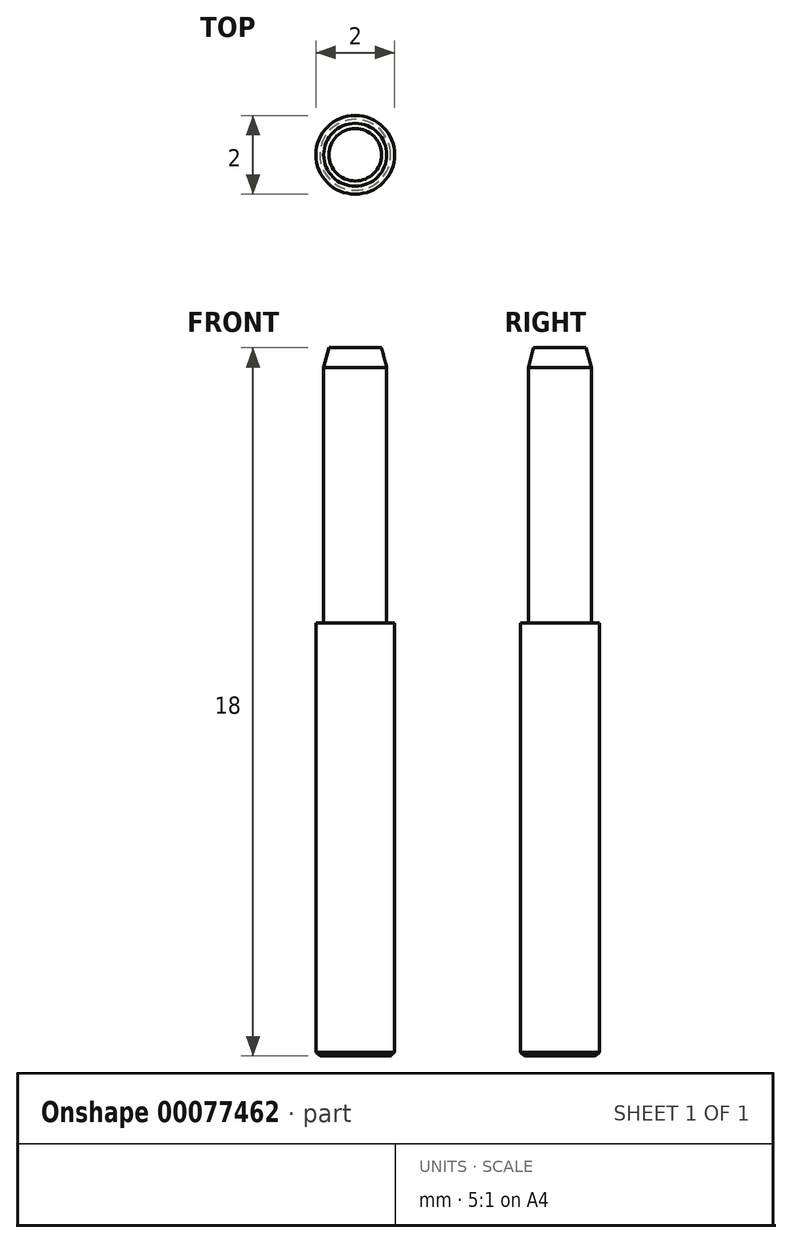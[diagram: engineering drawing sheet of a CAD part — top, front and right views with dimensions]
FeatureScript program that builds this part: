
annotation { "Feature Type Name" : "Feature", "Feature Type Description" : "" }
export const myFeature = defineFeature(function(context is Context, id is Id, definition is map)
    precondition{}
    {
        {
            var Q0;
            Q0=qCreatedBy(makeId("Top.planeOp"),FACE);
            var sketch = newSketch(context, id + "F0", { "sketchPlane" : qUnion([Q0])});
            skCircle(sketch, "E0", {"center": v(0, 0) * mm, "radius": 1 * mm});
            skSolve(sketch);
        }
        {
            var Q0;
            Q0=makeQuery(id+"F0.imprint","IMPRINT",FACE,{"disambiguationData":[TD([[makeQuery(id+"F0.imprint","IMPRINT",EDGE,{"derivedFrom":sQuery(id+"F0.wireOp",EDGE,"E0")}),1.0]])]});
            extrude(context, id + "F1", {"entities" : qUnion([Q0]), "depth" : 11 * mm});
        }
        {
            var Q0;
            Q0=makeQuery(id+"F1.opExtrude","CAP_FACE",FACE,{"disambiguationData":[OSD([sQuery(id+"F0.wireOp",EDGE,"E0")])],"isStart":false});
            var sketch = newSketch(context, id + "F2", { "sketchPlane" : qUnion([Q0])});
            skCircle(sketch, "E1", {"center": v(0, 0) * mm, "radius": 0.8 * mm});
            skSolve(sketch);
        }
        {
            var Q0;
            Q0=makeQuery(id+"F2.imprint","IMPRINT",FACE,{"disambiguationData":[TD([[makeQuery(id+"F2.imprint","IMPRINT",EDGE,{"derivedFrom":sQuery(id+"F2.wireOp",EDGE,"E1")}),1.0]])]});
            extrude(context, id + "F3", {"entities" : qUnion([Q0]), "operationType" : NewBodyOperationType.ADD, "depth" : 7 * mm});
        }
        {
            var Q0;
            Q0=makeQuery(id+"F1.opExtrude","CAP_EDGE",EDGE,{"disambiguationData":[OSD([sQuery(id+"F0.wireOp",EDGE,"E0")])],"isStart":true});
            chamfer(context, id + "F4", {"entities" : qUnion([Q0]), "width" : 0.1 * mm, "tangentPropagation" : true});
        }
        {
            var Q0;
            Q0=makeQuery(id+"F3.opExtrude","CAP_EDGE",EDGE,{"disambiguationData":[OSD([sQuery(id+"F2.wireOp",EDGE,"E1")])],"isStart":false});
            chamfer(context, id + "F5", {"entities" : qUnion([Q0]), "chamferType" : ChamferType.OFFSET_ANGLE, "width" : 0.5 * mm, "oppositeDirection" : true, "angle" : 15 * degree, "tangentPropagation" : true});
        }
    });
